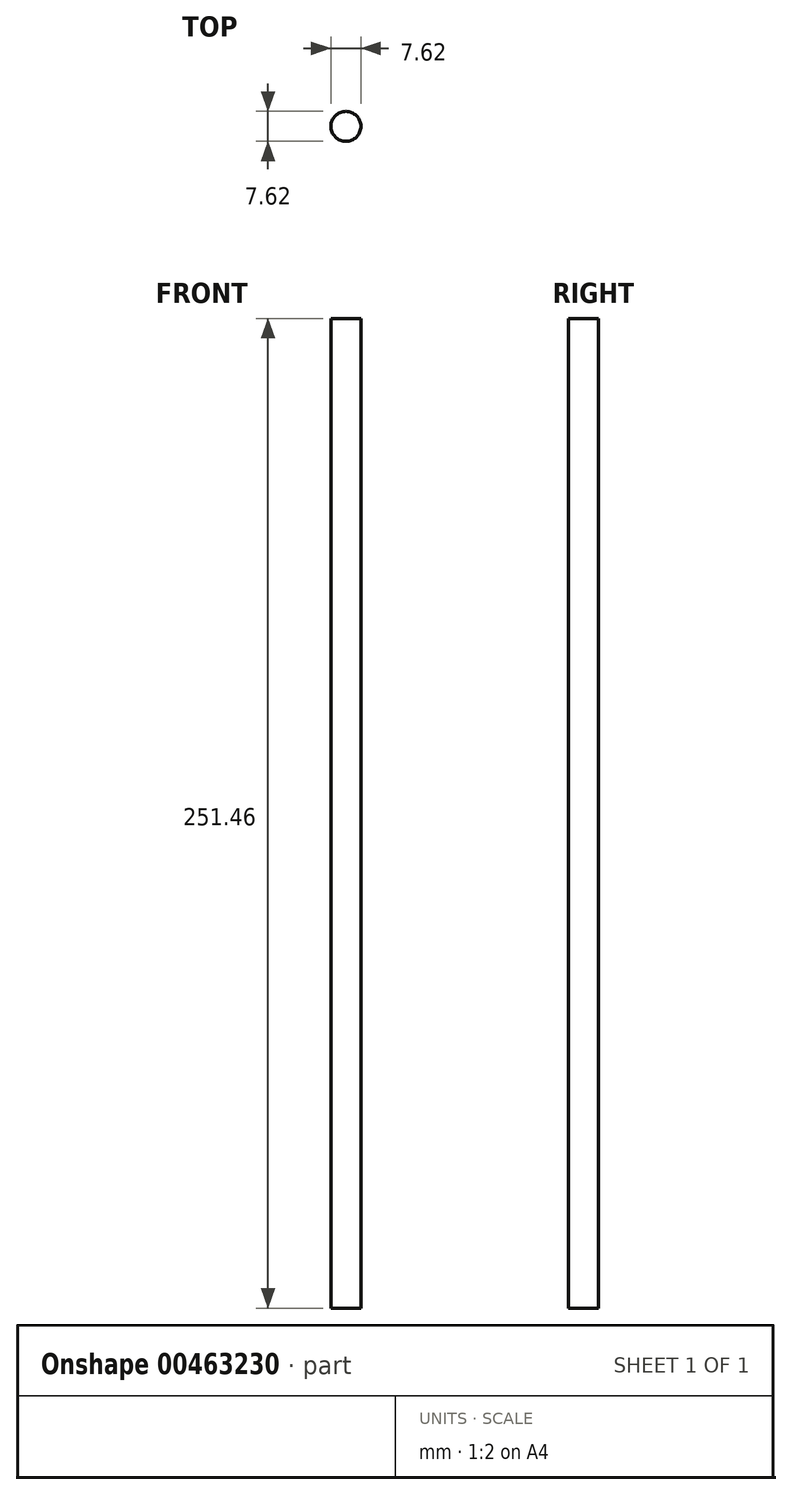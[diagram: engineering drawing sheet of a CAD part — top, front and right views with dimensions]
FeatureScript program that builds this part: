
annotation { "Feature Type Name" : "Feature", "Feature Type Description" : "" }
export const myFeature = defineFeature(function(context is Context, id is Id, definition is map)
    precondition{}
    {
        {
            var Q0;
            Q0=qCreatedBy(makeId("Top.planeOp"),FACE);
            var sketch = newSketch(context, id + "F0", { "sketchPlane" : qUnion([Q0])});
            skCircle(sketch, "E0", {"center": v(0, 0) * mm, "radius": 3.81 * mm});
            skSolve(sketch);
        }
        {
            var Q0;
            Q0=qSketchRegion(id+"F0",true);
            extrude(context, id + "F1", {"entities" : qUnion([Q0]), "endBound" : BoundingType.SYMMETRIC, "depth" : 251.46 * mm});
        }
    });
